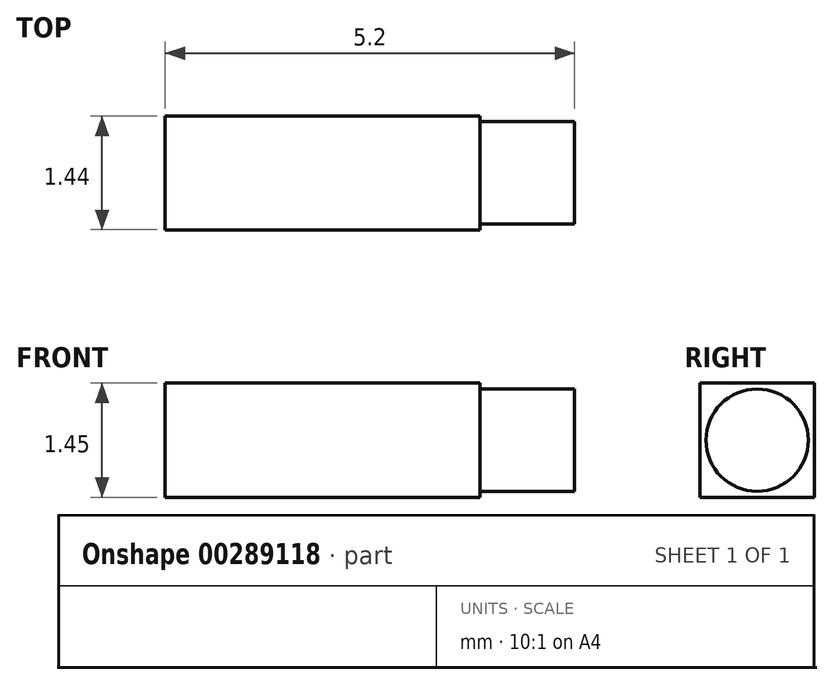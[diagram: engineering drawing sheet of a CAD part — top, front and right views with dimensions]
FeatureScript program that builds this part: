
annotation { "Feature Type Name" : "Feature", "Feature Type Description" : "" }
export const myFeature = defineFeature(function(context is Context, id is Id, definition is map)
    precondition{}
    {
        {
            var Q0;
            Q0=qCreatedBy(makeId("Top.planeOp"),FACE);
            var sketch = newSketch(context, id + "F0", { "sketchPlane" : qUnion([Q0])});
            skLineSegment(sketch, "E0.bottom", {"start": v(-9.31, -0.73) * mm, "end": v(-13.31, -0.73) * mm});
            skLineSegment(sketch, "E0.top", {"start": v(-9.31, 0.72) * mm, "end": v(-13.31, 0.72) * mm});
            skLineSegment(sketch, "E0.left", {"start": v(-9.31, -0.73) * mm, "end": v(-9.31, 0.72) * mm});
            skLineSegment(sketch, "E0.right", {"start": v(-13.31, -0.73) * mm, "end": v(-13.31, 0.72) * mm});
            skPoint(sketch, "E0.middle", {"position": v(-11.31, 0) * mm});
            skSolve(sketch);
        }
        {
            var Q0;
            Q0 = qSketchRegion(id + "F0", true);
            extrude(context, id + "F1", {"entities" : qUnion([Q0]), "depth" : 1.45 * mm, "offsetDistance" : 25 * mm});
        }
        {
            var Q0;
            Q0=makeQuery(id+"F1.opExtrude","SWEPT_FACE",FACE,{"disambiguationData":[OSD([sQuery(id+"F0.wireOp",EDGE,"E0.left")])]});
            var sketch = newSketch(context, id + "F2", { "sketchPlane" : qUnion([Q0])});
            skCircle(sketch, "E1", {"center": v(0, 0.72) * mm, "radius": 0.65 * mm});
            skPoint(sketch, "E1.centerSnap0", {"position": v(-0.73, 0.72) * mm});
            skSolve(sketch);
        }
        {
            var Q0;
            Q0 = qSketchRegion(id + "F2", true);
            extrude(context, id + "F3", {"entities" : qUnion([Q0]), "operationType" : NewBodyOperationType.ADD, "depth" : 1.2 * mm, "offsetDistance" : 25 * mm});
        }
    });
